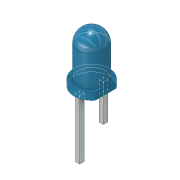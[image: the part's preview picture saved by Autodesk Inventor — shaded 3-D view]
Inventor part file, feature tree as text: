
AUTODESK INVENTOR PART (.ipt)
format: ipt  version: 2017 (Build 210142000, 142)  size: 148,992 bytes
history: native  units: in
note: dims shown in document units (in); Inventor stores cm internally (conversion verified against a paired STEP export)
features: sketch x4, extrude x3, revolve x1
ambient origin geometry x8: Origin, YZ Plane, XZ Plane, XY Plane, X Axis, Y Axis, Z Axis, Center Point
bodies: Solid1 (feature_tree)
feature tree (8):
  revolve  "Revolution1"  [1 undecoded]
  extrude  "Extrusion1"  Depth=0.0738in
  extrude  "Extrusion2"  Depth=0.1335in
  extrude  "Extrusion3"  Depth=0.25in TaperAngle=0.0deg
  sketch  "Sketch1"  dims[d0=0.057in d1=0.028in]
  sketch  "Sketch2"  dims[d2=0.0738in d3=0.2145in]
  sketch  "Sketch3"  dims[d4=90.0deg d5=0.1335in]
  sketch  "Sketch5"  dims[d6=1.0in d7=0.0in d11=0.25in d12=0.0in d13=0.018in d14=0.019in d15=0.119in d16=1.0in d17=0.0in]
note: 1 required parameter value undecoded (feature->parameter linkage not recoverable at this tier; creation-order binding heuristic only, values carry confidence <= 0.55)
